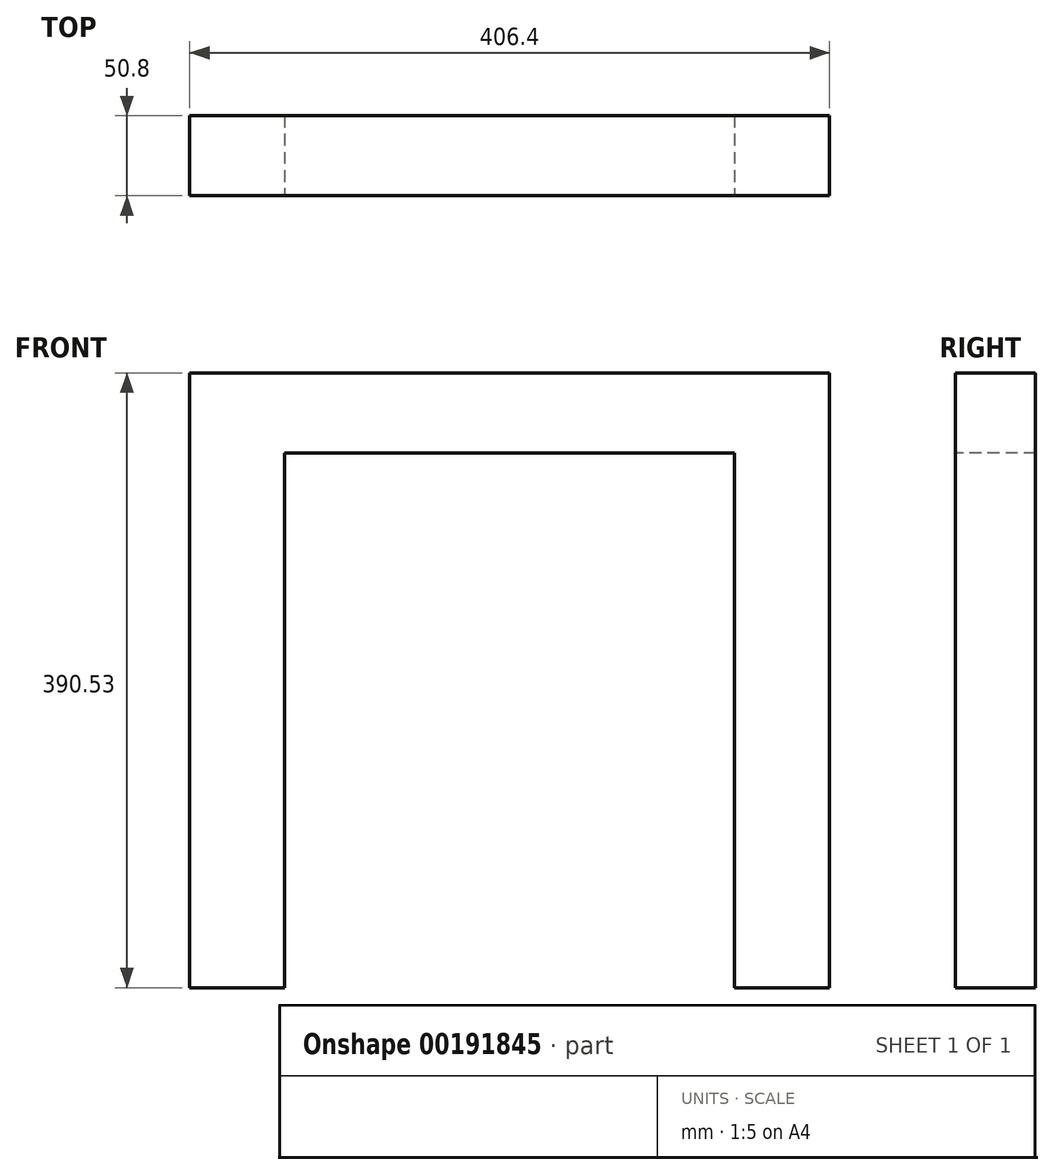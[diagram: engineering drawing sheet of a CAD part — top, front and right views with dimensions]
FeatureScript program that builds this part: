
annotation { "Feature Type Name" : "Feature", "Feature Type Description" : "" }
export const myFeature = defineFeature(function(context is Context, id is Id, definition is map)
    precondition{}
    {
        {
            var Q0;
            Q0=qCreatedBy(makeId("Front.planeOp"),FACE);
            var sketch = newSketch(context, id + "F0", { "sketchPlane" : qUnion([Q0])});
            skLineSegment(sketch, "E0.bottom", {"start": v(203.2, 0) * mm, "end": v(-203.2, 0) * mm});
            skLineSegment(sketch, "E0.top", {"start": v(203.2, 390.53) * mm, "end": v(-203.2, 390.53) * mm});
            skLineSegment(sketch, "E0.left", {"start": v(203.2, 0) * mm, "end": v(203.2, 390.52) * mm});
            skLineSegment(sketch, "E0.right", {"start": v(-203.2, 0) * mm, "end": v(-203.2, 390.53) * mm});
            skPoint(sketch, "E0.middle", {"position": v(0, 195.26) * mm});
            skSolve(sketch);
        }
        {
            var Q0;
            Q0 = qSketchRegion(id + "F0", true);
            extrude(context, id + "F1", {"entities" : qUnion([Q0]), "oppositeDirection" : true, "depth" : 50.8 * mm});
        }
        {
            var Q0;
            Q0=qCreatedBy(makeId("Front.planeOp"),FACE);
            var sketch = newSketch(context, id + "F2", { "sketchPlane" : qUnion([Q0])});
            skLineSegment(sketch, "E1.bottom", {"start": v(-142.87, 0) * mm, "end": v(142.87, 0) * mm});
            skLineSegment(sketch, "E1.top", {"start": v(-142.88, 339.73) * mm, "end": v(142.88, 339.73) * mm});
            skLineSegment(sketch, "E1.left", {"start": v(-142.87, 0) * mm, "end": v(-142.88, 339.73) * mm});
            skLineSegment(sketch, "E1.right", {"start": v(142.88, 0) * mm, "end": v(142.88, 339.73) * mm});
            skSolve(sketch);
        }
        {
            var Q0;
            Q0=makeQuery(id+"F2.imprint","IMPRINT",FACE,{"disambiguationData":[TD([[makeQuery(id+"F2.imprint","IMPRINT",EDGE,{"derivedFrom":sQuery(id+"F2.wireOp",EDGE,"E1.bottom")}),1.0]])]});
            extrude(context, id + "F3", {"entities" : qUnion([Q0]), "operationType" : NewBodyOperationType.REMOVE, "endBound" : BoundingType.UP_TO_NEXT, "oppositeDirection" : true, "depth" : 25.4 * mm});
        }
    });
